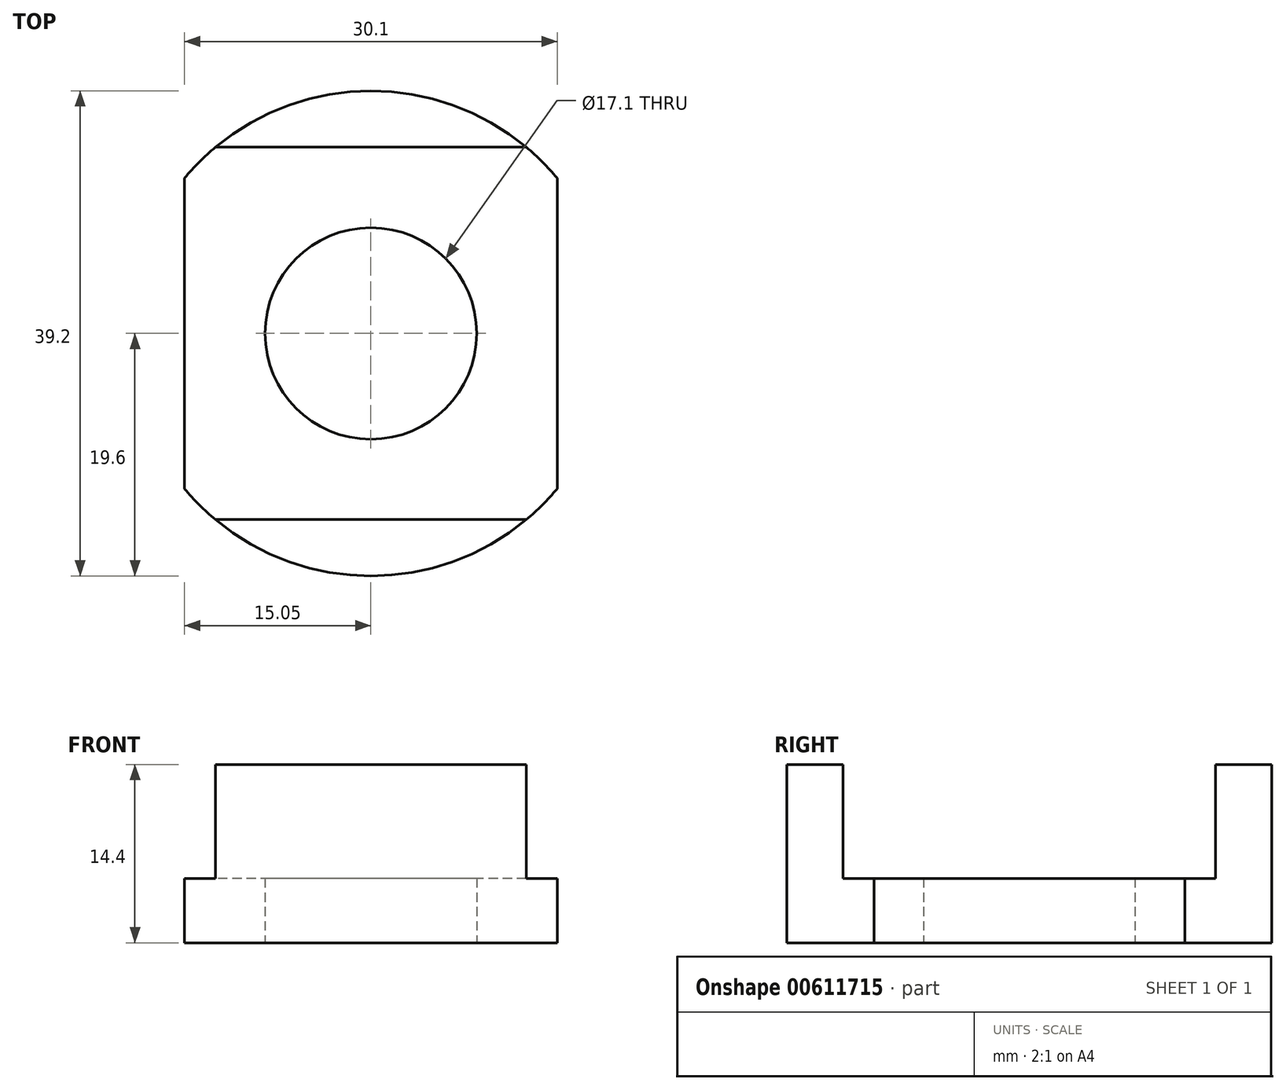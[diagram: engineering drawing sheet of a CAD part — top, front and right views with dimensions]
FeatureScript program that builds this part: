
annotation { "Feature Type Name" : "Feature", "Feature Type Description" : "" }
export const myFeature = defineFeature(function(context is Context, id is Id, definition is map)
    precondition{}
    {
        {
            var Q0;
            Q0=qCreatedBy(makeId("Top.planeOp"),FACE);
            var sketch = newSketch(context, id + "F0", { "sketchPlane" : qUnion([Q0])});
            skCircle(sketch, "E0", {"center": v(0, 0) * mm, "radius": 8.55 * mm});
            skCircle(sketch, "E1", {"center": v(0, 0) * mm, "radius": 19.6 * mm});
            skSolve(sketch);
        }
        {
            var Q0;
            Q0=makeQuery(id+"F0.imprint","IMPRINT",FACE,{"disambiguationData":[TD([[makeQuery(id+"F0.imprint","IMPRINT",EDGE,{"derivedFrom":sQuery(id+"F0.wireOp",EDGE,"E0")}),-1.0]])]});
            extrude(context, id + "F1", {"entities" : qUnion([Q0]), "depth" : 5.2 * mm, "offsetDistance" : 25 * mm});
        }
        {
            var Q0;
            Q0=makeQuery(id+"F1.opExtrude","CAP_FACE",FACE,{"disambiguationData":[OSD([sQuery(id+"F0.wireOp",EDGE,"E0"),sQuery(id+"F0.wireOp",EDGE,"E1")])],"isStart":false});
            var sketch = newSketch(context, id + "F2", { "sketchPlane" : qUnion([Q0])});
            skLineSegment(sketch, "E2.bottom", {"start": v(15.05, -15.05) * mm, "end": v(-15.05, -15.05) * mm});
            skLineSegment(sketch, "E2.top", {"start": v(15.05, 15.05) * mm, "end": v(-15.05, 15.05) * mm});
            skLineSegment(sketch, "E2.left", {"start": v(15.05, -15.05) * mm, "end": v(15.05, 15.05) * mm});
            skLineSegment(sketch, "E2.right", {"start": v(-15.05, -15.05) * mm, "end": v(-15.05, 15.05) * mm});
            skPoint(sketch, "E2.middle", {"position": v(0, 0) * mm});
            skSolve(sketch);
        }
        {
            var Q0;
            {var subQ0=sQuery(id+"F2.wireOp",EDGE,"E2.top");var subQ1=makeQuery(id+"F1.opExtrude","CAP_EDGE",EDGE,{"disambiguationData":[OSD([sQuery(id+"F0.wireOp",EDGE,"E1")])],"isStart":false});var subQ2=makeQuery(id+"F2.imprint","INTERSECT",VERTEX,{"disambiguationData":[OD(0.0)],"derivedFrom":[subQ1,subQ0]});Q0=makeQuery(id+"F2.imprint","IMPRINT",FACE,{"disambiguationData":[TD([[makeQuery(id+"F2.imprint","IMPRINT",EDGE,{"disambiguationData":[TD([[subQ2,-1.0]])],"derivedFrom":subQ0}),-1.0]])]});}
            var Q1;
            {var subQ0=sQuery(id+"F2.wireOp",EDGE,"E2.bottom");var subQ1=makeQuery(id+"F1.opExtrude","CAP_EDGE",EDGE,{"disambiguationData":[OSD([sQuery(id+"F0.wireOp",EDGE,"E1")])],"isStart":false});var subQ2=makeQuery(id+"F2.imprint","INTERSECT",VERTEX,{"disambiguationData":[OD(0.0)],"derivedFrom":[subQ1,subQ0]});Q1=makeQuery(id+"F2.imprint","IMPRINT",FACE,{"disambiguationData":[TD([[makeQuery(id+"F2.imprint","IMPRINT",EDGE,{"disambiguationData":[TD([[subQ2,-1.0]])],"derivedFrom":subQ0}),1.0]])]});}
            extrude(context, id + "F3", {"entities" : qUnion([Q0, Q1]), "operationType" : NewBodyOperationType.ADD, "depth" : 9.2 * mm, "offsetDistance" : 25 * mm});
        }
        {
            var Q0;
            {var subQ0=sQuery(id+"F2.wireOp",EDGE,"E2.right");var subQ1=makeQuery(id+"F1.opExtrude","CAP_EDGE",EDGE,{"disambiguationData":[OSD([sQuery(id+"F0.wireOp",EDGE,"E1")])],"isStart":false});var subQ2=makeQuery(id+"F2.imprint","INTERSECT",VERTEX,{"disambiguationData":[OD(0.0)],"derivedFrom":[subQ1,subQ0]});Q0=makeQuery(id+"F2.imprint","IMPRINT",FACE,{"disambiguationData":[TD([[makeQuery(id+"F2.imprint","IMPRINT",EDGE,{"disambiguationData":[TD([[subQ2,-1.0]])],"derivedFrom":subQ0}),1.0]])]});}
            var Q1;
            {var subQ0=sQuery(id+"F2.wireOp",EDGE,"E2.left");var subQ1=makeQuery(id+"F1.opExtrude","CAP_EDGE",EDGE,{"disambiguationData":[OSD([sQuery(id+"F0.wireOp",EDGE,"E1")])],"isStart":false});var subQ2=makeQuery(id+"F2.imprint","INTERSECT",VERTEX,{"disambiguationData":[OD(0.0)],"derivedFrom":[subQ1,subQ0]});Q1=makeQuery(id+"F2.imprint","IMPRINT",FACE,{"disambiguationData":[TD([[makeQuery(id+"F2.imprint","IMPRINT",EDGE,{"disambiguationData":[TD([[subQ2,-1.0]])],"derivedFrom":subQ0}),-1.0]])]});}
            extrude(context, id + "F4", {"entities" : qUnion([Q0, Q1]), "operationType" : NewBodyOperationType.REMOVE, "endBound" : BoundingType.THROUGH_ALL, "oppositeDirection" : true, "depth" : 25 * mm, "offsetDistance" : 25 * mm});
        }
    });
